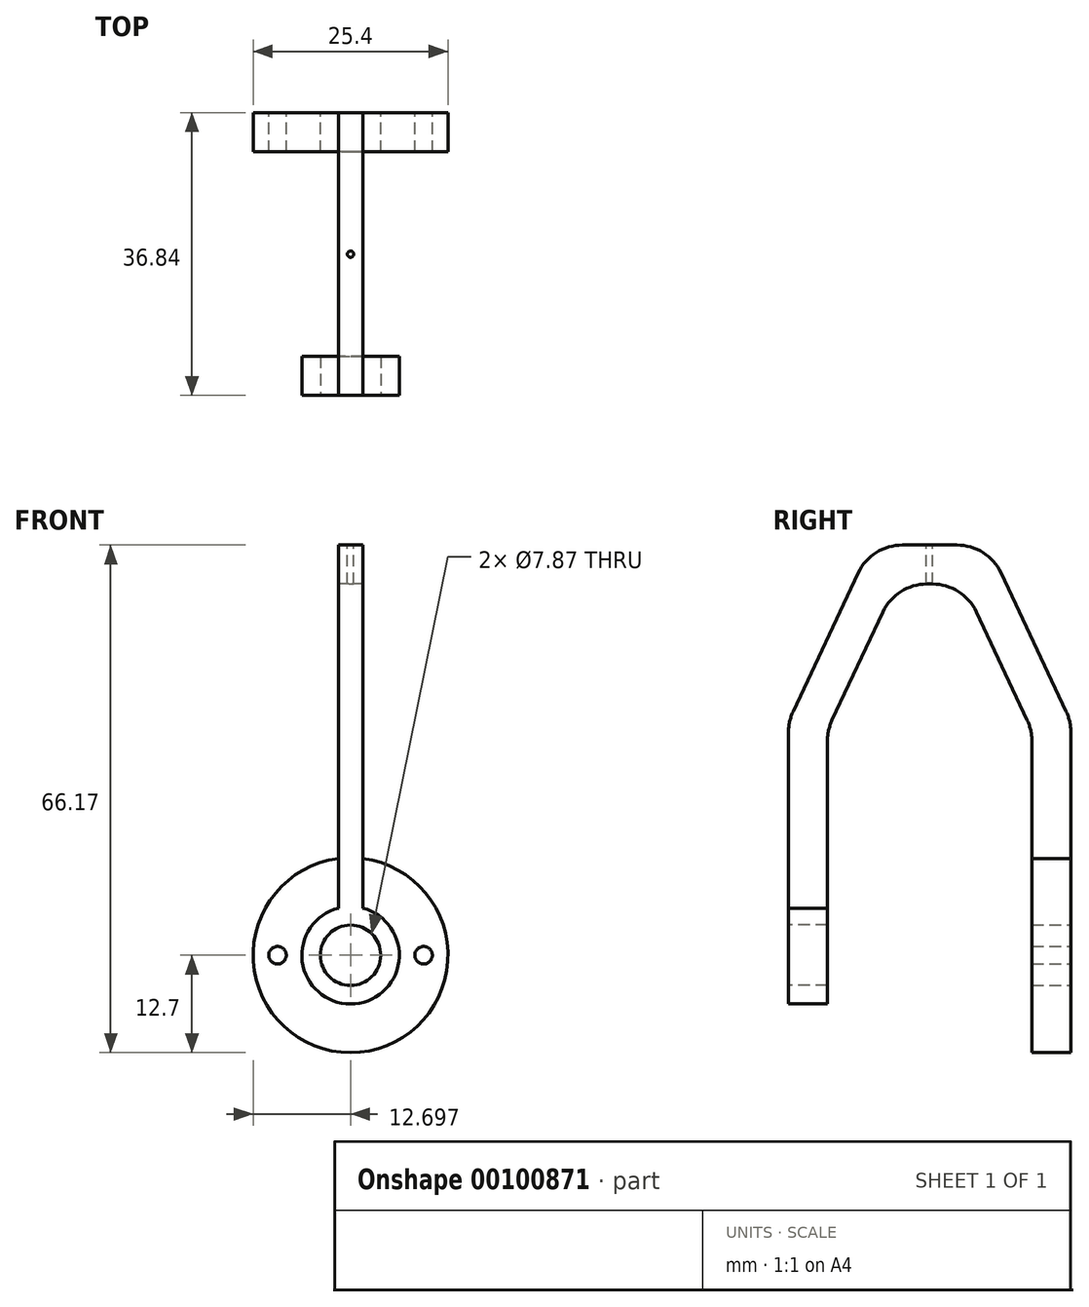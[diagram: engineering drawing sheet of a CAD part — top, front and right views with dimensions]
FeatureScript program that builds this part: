
annotation { "Feature Type Name" : "Feature", "Feature Type Description" : "" }
export const myFeature = defineFeature(function(context is Context, id is Id, definition is map)
    precondition{}
    {
        {
            var Q0;
            Q0=qCreatedBy(makeId("Right.planeOp"),FACE);
            var sketch = newSketch(context, id + "F0", { "sketchPlane" : qUnion([Q0])});
            skLineSegment(sketch, "E0", {"start": v(-13.33, 5.13) * mm, "end": v(-13.33, 29.1) * mm});
            skLineSegment(sketch, "E1", {"start": v(-12.73, 31.81) * mm, "end": v(-6.09, 45.93) * mm});
            skLineSegment(sketch, "E2", {"start": v(-0.34, 49.58) * mm, "end": v(0, 49.58) * mm});
            skLineSegment(sketch, "E3", {"start": v(0, 54.66) * mm, "end": v(-3.56, 54.66) * mm});
            skLineSegment(sketch, "E4", {"start": v(-9.3, 51.01) * mm, "end": v(-17.81, 32.95) * mm});
            skLineSegment(sketch, "E5", {"start": v(-18.42, 30.24) * mm, "end": v(-18.41, 5.13) * mm});
            skLineSegment(sketch, "E6", {"start": v(-18.41, 5.13) * mm, "end": v(-13.34, 5.13) * mm});
            skLineSegment(sketch, "E7", {"start": v(0, 0) * mm, "end": v(0, 16.88) * mm, "construction": true});
            skPoint(sketch, "E8.visualSharp", {"position": v(-7.6, 54.66) * mm});
            skArc(sketch, "E8.filletArc", {"start": v(-3.56, 54.66) * mm, "mid": v(-6.97, 53.67) * mm, "end": v(-9.3, 51.01) * mm});
            skPoint(sketch, "E9.visualSharp", {"position": v(-18.42, 31.66) * mm});
            skArc(sketch, "E9.filletArc", {"start": v(-17.81, 32.95) * mm, "mid": v(-18.26, 31.63) * mm, "end": v(-18.41, 30.24) * mm});
            skPoint(sketch, "E10.visualSharp", {"position": v(-13.33, 30.53) * mm});
            skArc(sketch, "E10.filletArc", {"start": v(-12.73, 31.81) * mm, "mid": v(-13.18, 30.5) * mm, "end": v(-13.34, 29.1) * mm});
            skPoint(sketch, "E11.visualSharp", {"position": v(-4.37, 49.58) * mm});
            skArc(sketch, "E11.filletArc", {"start": v(-0.34, 49.58) * mm, "mid": v(-3.74, 48.59) * mm, "end": v(-6.09, 45.93) * mm});
            skLineSegment(sketch, "E12.MirrorCS", {"start": v(0.34, 49.58) * mm, "end": v(0, 49.58) * mm});
            skArc(sketch, "E13.MirrorCS", {"start": v(12.73, 31.81) * mm, "mid": v(13.18, 30.5) * mm, "end": v(13.34, 29.1) * mm});
            skArc(sketch, "E14.MirrorCS", {"start": v(17.81, 32.95) * mm, "mid": v(18.26, 31.63) * mm, "end": v(18.41, 30.24) * mm});
            skArc(sketch, "E15.MirrorCS", {"start": v(0.34, 49.58) * mm, "mid": v(3.74, 48.59) * mm, "end": v(6.09, 45.93) * mm});
            skPoint(sketch, "E16.MirrorP", {"position": v(7.6, 54.66) * mm});
            skPoint(sketch, "E17.MirrorP", {"position": v(18.42, 31.66) * mm});
            skLineSegment(sketch, "E18.MirrorCS", {"start": v(13.33, 5.13) * mm, "end": v(13.33, 29.1) * mm});
            skLineSegment(sketch, "E19.MirrorCS", {"start": v(0, 54.66) * mm, "end": v(3.56, 54.66) * mm});
            skPoint(sketch, "E20.MirrorP", {"position": v(13.33, 30.53) * mm});
            skLineSegment(sketch, "E21.MirrorCS", {"start": v(18.41, 5.13) * mm, "end": v(13.34, 5.13) * mm});
            skArc(sketch, "E22.MirrorCS", {"start": v(3.56, 54.66) * mm, "mid": v(6.97, 53.67) * mm, "end": v(9.3, 51.01) * mm});
            skPoint(sketch, "E23.MirrorP", {"position": v(4.37, 49.58) * mm});
            skLineSegment(sketch, "E24.MirrorCS", {"start": v(9.3, 51.01) * mm, "end": v(17.81, 32.95) * mm});
            skLineSegment(sketch, "E25.MirrorCS", {"start": v(12.73, 31.81) * mm, "end": v(6.09, 45.93) * mm});
            skLineSegment(sketch, "E26.MirrorCS", {"start": v(18.42, 30.24) * mm, "end": v(18.41, 5.13) * mm});
            skSolve(sketch);
        }
        {
            var Q0;
            Q0 = qSketchRegion(id + "F0", true);
            extrude(context, id + "F1", {"entities" : qUnion([Q0]), "depth" : 3.17 * mm});
        }
        {
            var Q0;
            Q0=makeQuery(id+"F1.opExtrude","SWEPT_FACE",FACE,{"disambiguationData":[OSD([sQuery(id+"F0.wireOp",EDGE,"E5")])]});
            var sketch = newSketch(context, id + "F2", { "sketchPlane" : qUnion([Q0])});
            skCircle(sketch, "E27", {"center": v(1.59, 1.19) * mm, "radius": 3.94 * mm});
            skPoint(sketch, "E27.centerSnap0", {"position": v(1.59, 5.13) * mm});
            skCircle(sketch, "E28", {"center": v(1.59, 1.19) * mm, "radius": 6.35 * mm});
            skSolve(sketch);
        }
        {
            var Q0;
            Q0 = qSketchRegion(id + "F2", true);
            var Q1;
            Q1=makeQuery(id+"F1.opExtrude","SWEPT_FACE",FACE,{"disambiguationData":[OSD([sQuery(id+"F0.wireOp",EDGE,"E0")])]});
            extrude(context, id + "F3", {"entities" : qUnion([Q0]), "operationType" : NewBodyOperationType.ADD, "endBound" : BoundingType.UP_TO_SURFACE, "oppositeDirection" : true, "endBoundEntityFace" : qUnion([Q1]), "depth" : 25.4 * mm});
        }
        {
            var Q0;
            Q0=makeQuery(id+"F1.opExtrude","SWEPT_FACE",FACE,{"disambiguationData":[OSD([sQuery(id+"F0.wireOp",EDGE,"E26.MirrorCS")])]});
            var sketch = newSketch(context, id + "F4", { "sketchPlane" : qUnion([Q0])});
            skCircle(sketch, "E29", {"center": v(-1.59, 1.19) * mm, "radius": 3.94 * mm});
            skCircle(sketch, "E30", {"center": v(-1.59, 1.19) * mm, "radius": 12.7 * mm});
            skCircle(sketch, "E31", {"center": v(-11.11, 1.19) * mm, "radius": 1.14 * mm});
            skCircle(sketch, "E32", {"center": v(7.94, 1.19) * mm, "radius": 1.14 * mm});
            skLineSegment(sketch, "E33", {"start": v(-11.11, 1.19) * mm, "end": v(7.94, 1.19) * mm, "construction": true});
            skSolve(sketch);
        }
        {
            var Q0;
            Q0 = qSketchRegion(id + "F4", true);
            var Q1;
            Q1=makeQuery(id+"F1.opExtrude","SWEPT_FACE",FACE,{"disambiguationData":[OSD([sQuery(id+"F0.wireOp",EDGE,"E18.MirrorCS")])]});
            extrude(context, id + "F5", {"entities" : qUnion([Q0]), "operationType" : NewBodyOperationType.ADD, "endBound" : BoundingType.UP_TO_SURFACE, "oppositeDirection" : true, "endBoundEntityFace" : qUnion([Q1]), "depth" : 25.4 * mm});
        }
        {
            var Q0;
            Q0=makeQuery(id+"F1.opExtrude","SWEPT_FACE",FACE,{"disambiguationData":[OSD([sQuery(id+"F0.wireOp",EDGE,"E3"),sQuery(id+"F0.wireOp",EDGE,"E19.MirrorCS")])]});
            var sketch = newSketch(context, id + "F6", { "sketchPlane" : qUnion([Q0])});
            skCircle(sketch, "E34", {"center": v(1.59, 0) * mm, "radius": 0.41 * mm});
            skLineSegment(sketch, "E35", {"start": v(0, 3.56) * mm, "end": v(3.18, -3.56) * mm, "construction": true});
            skSolve(sketch);
        }
        {
            var Q0;
            Q0 = qSketchRegion(id + "F6", true);
            extrude(context, id + "F7", {"entities" : qUnion([Q0]), "operationType" : NewBodyOperationType.REMOVE, "endBound" : BoundingType.UP_TO_NEXT, "oppositeDirection" : true, "depth" : 25.4 * mm});
        }
    });
